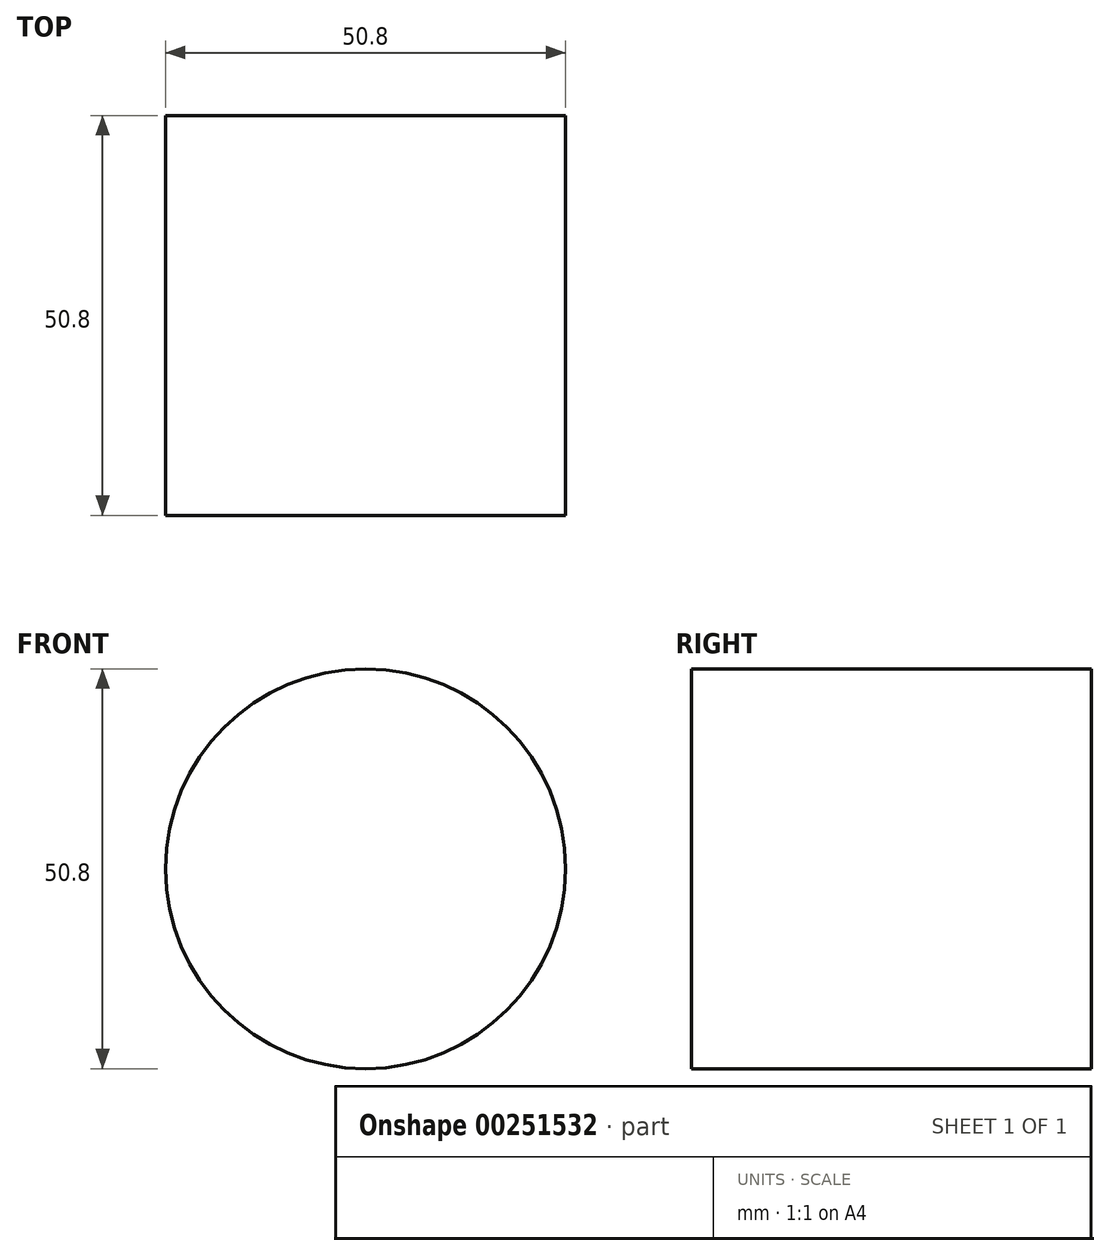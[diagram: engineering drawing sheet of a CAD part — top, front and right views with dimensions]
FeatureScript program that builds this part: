
annotation { "Feature Type Name" : "Feature", "Feature Type Description" : "" }
export const myFeature = defineFeature(function(context is Context, id is Id, definition is map)
    precondition{}
    {
        {
            var Q0;
            Q0=qCreatedBy(makeId("Front.planeOp"),FACE);
            var sketch = newSketch(context, id + "F0", { "sketchPlane" : qUnion([Q0])});
            skCircle(sketch, "E0", {"center": v(0, 0) * mm, "radius": 25.4 * mm});
            skSolve(sketch);
        }
        {
            var Q0;
            Q0 = qSketchRegion(id + "F0", true);
            extrude(context, id + "F1", {"entities" : qUnion([Q0]), "depth" : 50.8 * mm});
        }
    });
